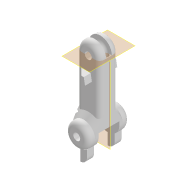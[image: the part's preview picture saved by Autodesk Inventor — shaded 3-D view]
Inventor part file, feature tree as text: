
AUTODESK INVENTOR PART (.ipt)
format: ipt  version: 2020.2 (Build 242310000, 310)  size: 329,216 bytes
history: native  units: mm
features: sketch x9, extrude x5, mirror x3, plane x2, chamfer x2, fillet x2, thread x1, sweep x1
ambient origin geometry x8: Origin, YZ Plane, XZ Plane, XY Plane, X Axis, Y Axis, Z Axis, Center Point
bodies: Solid1 (feature_tree)
feature tree (25):
  extrude  "base"  Depth=10.0mm
  extrude  "joint"  Depth=3.0mm
  plane  "Work Plane1"
  mirror  "Mirror1"
  chamfer  "Chamfer1"  Distance=8.0mm
  extrude  "joint_2"  Depth=10.0mm
  fillet  "Fillet1"  Radius=5.0mm
  plane  "Work Plane2"
  thread  "thread_hole_end"  [1 undecoded]
  extrude  "lock_1"  Depth=9.0mm TaperAngle=0.0deg
  mirror  "Mirror2"
  fillet  "Fillet3"  Radius=2.0mm
  extrude  "lock_2"  Depth=5.25mm
  mirror  "Mirror3"
  chamfer  "Chamfer2"  Distance=25.0mm
  sweep  "Sweep1"
  sketch  "Sketch1"  dims[d0=3.0mm d1=10.0mm]
  sketch  "Sketch2"  dims[d2=28.0mm d3=3.0mm]
  sketch  "Sketch3"  dims[d4=10.0mm d5=8.0mm d6=0.0mm]
  sketch  "Sketch5"  dims[d7=3.0mm d8=10.0mm d9=5.0mm d10=0.0mm d11=2.0mm d12=2.0mm d13=45.0deg]
  sketch  "Sketch6"  dims[d14=10.5mm d15=9.0mm d16=0.0mm d17=2.0mm]
  sketch  "Sketch8"  dims[d21=10.0mm d22=5.25mm]
  sketch  "Sketch9"  dims[d23=3.5mm]
  sketch  "Sketch10"  dims[d24=3.5mm]
  sketch  "Sketch11"  dims[d26=2.5mm d27=25.0mm d28=0.0mm d29=3.5mm d30=2.5mm d31=180.0deg d35=5.0mm d36=3.0mm d37=3.0mm d38=0.0mm d40=3.0mm d41=6.0mm d42=3.0mm d43=13.962634mm d44=3.0mm d45=0.0mm d46=3.0mm d47=2.0mm d48=45.0deg d49=3.5mm d50=10.0mm d52=3.5mm d54=3.0mm d55=0.0mm d56=0.0mm]
note: 1 required parameter value undecoded (feature->parameter linkage not recoverable at this tier; creation-order binding heuristic only, values carry confidence <= 0.55)
